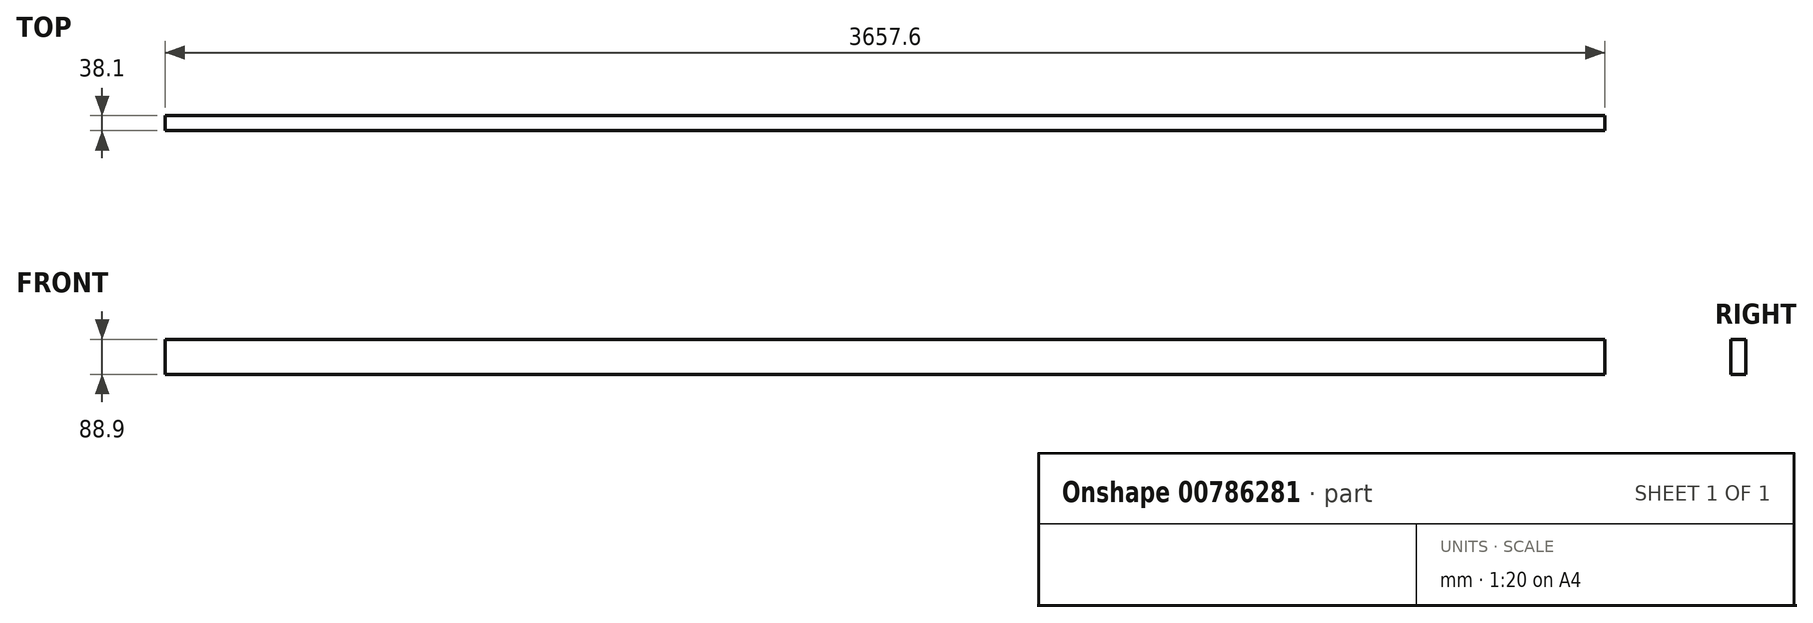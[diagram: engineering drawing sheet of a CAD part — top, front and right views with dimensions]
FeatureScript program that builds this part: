
annotation { "Feature Type Name" : "Feature", "Feature Type Description" : "" }
export const myFeature = defineFeature(function(context is Context, id is Id, definition is map)
    precondition{}
    {
        {
            var Q0;
            Q0=qCreatedBy(makeId("Front.planeOp"),FACE);
            var sketch = newSketch(context, id + "F0", { "sketchPlane" : qUnion([Q0])});
            skLineSegment(sketch, "E0.bottom", {"start": v(-1828.8, 44.45) * mm, "end": v(1828.8, 44.45) * mm});
            skLineSegment(sketch, "E0.top", {"start": v(-1828.8, -44.45) * mm, "end": v(1828.8, -44.45) * mm});
            skLineSegment(sketch, "E0.left", {"start": v(-1828.8, 44.45) * mm, "end": v(-1828.8, -44.45) * mm});
            skLineSegment(sketch, "E0.right", {"start": v(1828.8, 44.45) * mm, "end": v(1828.8, -44.45) * mm});
            skPoint(sketch, "E0.middle", {"position": v(0, 0) * mm});
            skSolve(sketch);
        }
        {
            var Q0;
            Q0=makeQuery(id+"F0.imprint","IMPRINT",FACE,{"disambiguationData":[TD([[makeQuery(id+"F0.imprint","IMPRINT",EDGE,{"derivedFrom":sQuery(id+"F0.wireOp",EDGE,"E0.bottom")}),-1.0]])]});
            extrude(context, id + "F1", {"entities" : qUnion([Q0]), "endBound" : BoundingType.SYMMETRIC, "depth" : 38.1 * mm, "offsetDistance" : 25.4 * mm});
        }
    });
